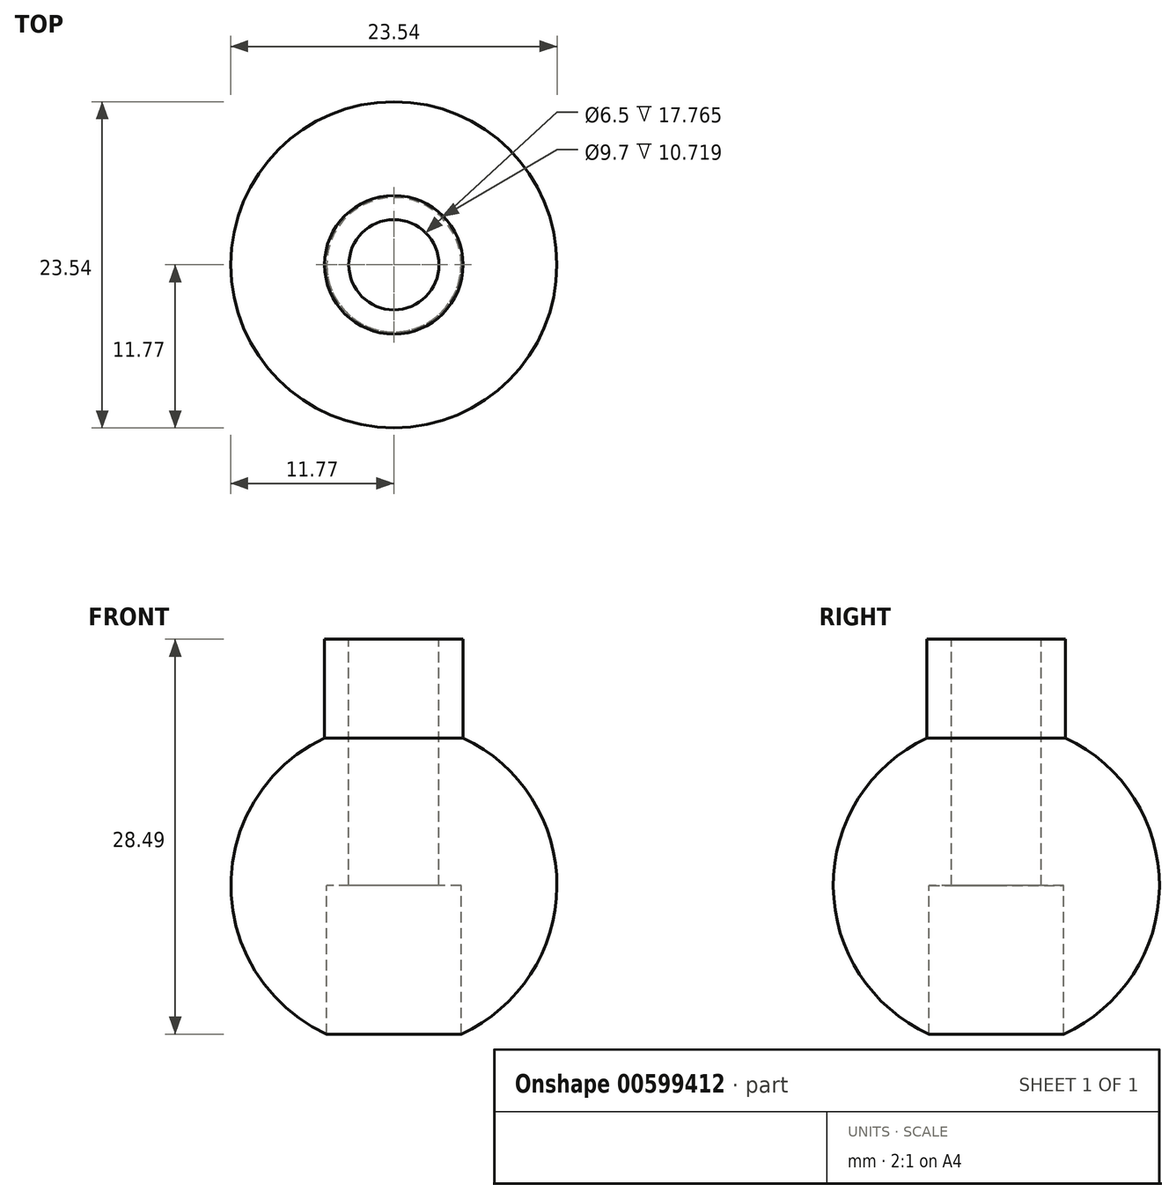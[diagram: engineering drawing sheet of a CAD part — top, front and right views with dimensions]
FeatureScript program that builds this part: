
annotation { "Feature Type Name" : "Feature", "Feature Type Description" : "" }
export const myFeature = defineFeature(function(context is Context, id is Id, definition is map)
    precondition{}
    {
        {
            var Q0;
            Q0=qCreatedBy(makeId("Front.planeOp"),FACE);
            var sketch = newSketch(context, id + "F0", { "sketchPlane" : qUnion([Q0])});
            skLineSegment(sketch, "E0.bottom", {"start": v(0, 0) * mm, "end": v(-5, 0) * mm});
            skLineSegment(sketch, "E0.top", {"start": v(0, 17.77) * mm, "end": v(-5, 17.77) * mm});
            skLineSegment(sketch, "E0.left", {"start": v(0, 0) * mm, "end": v(0, 17.77) * mm});
            skLineSegment(sketch, "E0.right", {"start": v(-5, 0) * mm, "end": v(-5, 17.77) * mm});
            skArc(sketch, "E1", {"start": v(0, 11.77) * mm, "mid": v(-11.77, 0) * mm, "end": v(0, -11.77) * mm});
            skLineSegment(sketch, "E2", {"start": v(0, 0) * mm, "end": v(0, -11.77) * mm});
            skSolve(sketch);
        }
        {
            var Q0;
            Q0=qSketchRegion(id+"F0",true);
            var Q1;
            Q1=sQuery(id+"F0.wireOp",EDGE,"E0.left");
            revolve(context, id + "F1", {"entities" : qUnion([Q0]), "axis" : qUnion([Q1]), "revolveType" : RevolveType.FULL});
        }
        {
            var Q0;
            Q0=makeQuery(id+"F1.opRevolve","SWEPT_FACE",FACE,{"disambiguationData":[OSD([sQuery(id+"F0.wireOp",EDGE,"E0.top")])]});
            var sketch = newSketch(context, id + "F2", { "sketchPlane" : qUnion([Q0])});
            skCircle(sketch, "E3", {"center": v(0, 0) * mm, "radius": 3.25 * mm});
            skSolve(sketch);
        }
        {
            var Q0;
            Q0=qSketchRegion(id+"F2",true);
            extrude(context, id + "F3", {"entities" : qUnion([Q0]), "operationType" : NewBodyOperationType.REMOVE, "endBound" : BoundingType.THROUGH_ALL, "oppositeDirection" : true, "depth" : 25 * mm, "offsetDistance" : 25 * mm});
        }
        {
            var Q0;
            Q0=qCreatedBy(makeId("Top.planeOp"),FACE);
            var sketch = newSketch(context, id + "F4", { "sketchPlane" : qUnion([Q0])});
            skCircle(sketch, "E4", {"center": v(0, 0) * mm, "radius": 4.85 * mm});
            skSolve(sketch);
        }
        {
            var Q0;
            Q0=qSketchRegion(id+"F4",true);
            extrude(context, id + "F5", {"entities" : qUnion([Q0]), "operationType" : NewBodyOperationType.REMOVE, "oppositeDirection" : true, "depth" : 25 * mm, "offsetDistance" : 25 * mm});
        }
    });
